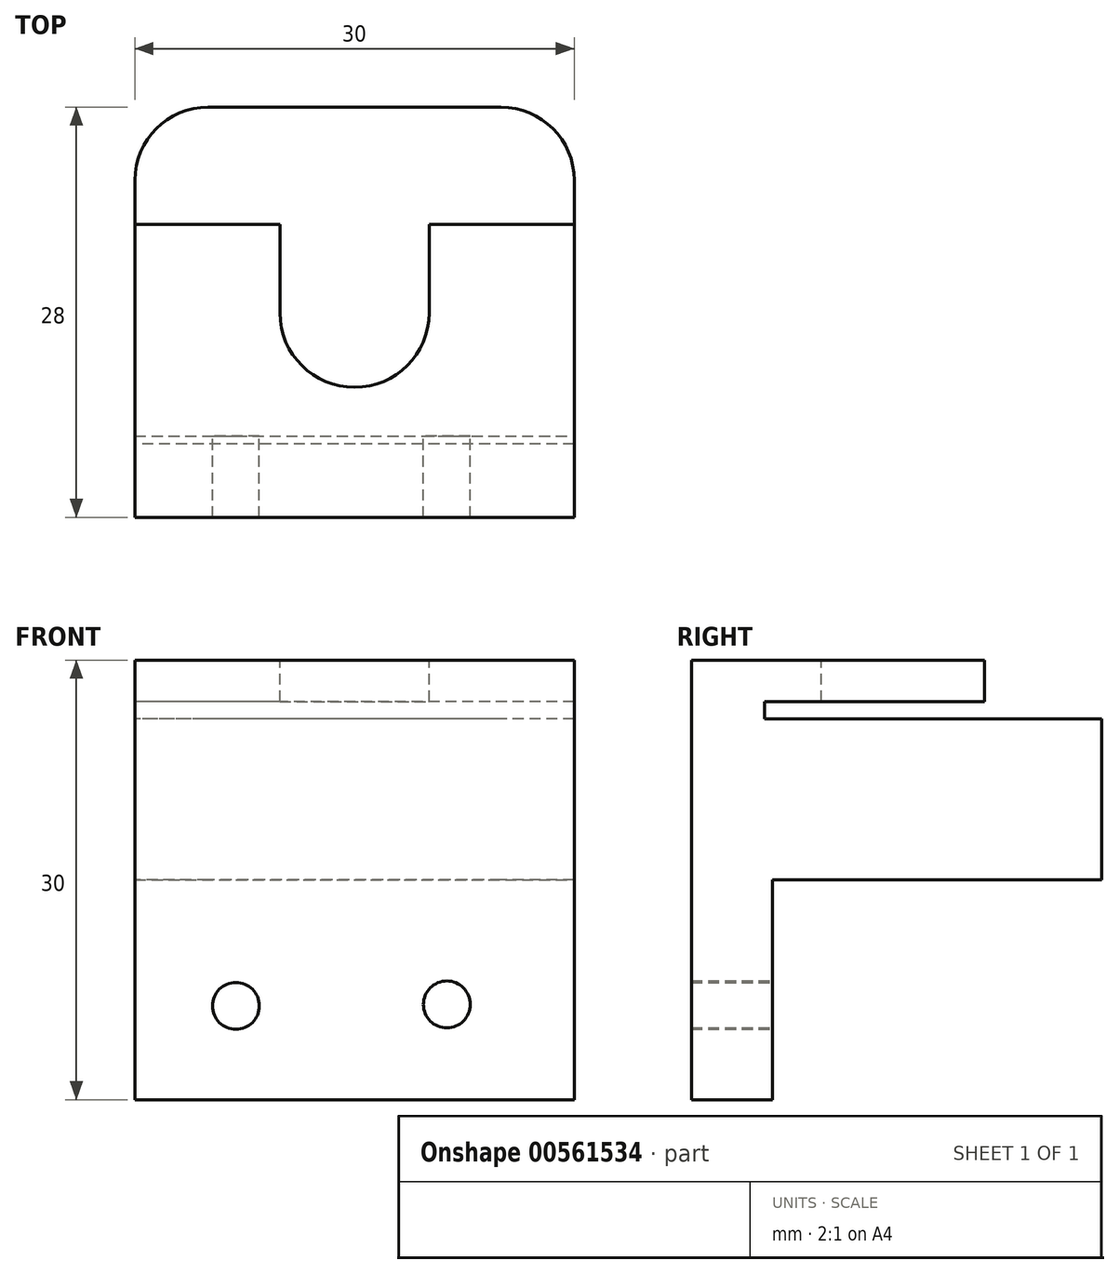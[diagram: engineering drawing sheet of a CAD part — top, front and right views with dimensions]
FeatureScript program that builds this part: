
annotation { "Feature Type Name" : "Feature", "Feature Type Description" : "" }
export const myFeature = defineFeature(function(context is Context, id is Id, definition is map)
    precondition{}
    {
        {
            var Q0;
            Q0=qCreatedBy(makeId("Top.planeOp"),FACE);
            var sketch = newSketch(context, id + "F0", { "sketchPlane" : qUnion([Q0])});
            skLineSegment(sketch, "E0.bottom", {"start": v(15, 14) * mm, "end": v(-15, 14) * mm});
            skLineSegment(sketch, "E0.top", {"start": v(15, -14) * mm, "end": v(-15, -14) * mm});
            skLineSegment(sketch, "E0.left", {"start": v(15, 14) * mm, "end": v(15, -14) * mm});
            skLineSegment(sketch, "E0.right", {"start": v(-15, 14) * mm, "end": v(-15, -14) * mm});
            skPoint(sketch, "E0.middle", {"position": v(0, 0) * mm});
            skSolve(sketch);
        }
        {
            var Q0;
            Q0=qSketchRegion(id+"F0",true);
            extrude(context, id + "F1", {"entities" : qUnion([Q0]), "depth" : 11 * mm, "offsetDistance" : 25 * mm});
        }
        {
            var Q0;
            Q0=makeQuery(id+"F1.opExtrude","SWEPT_EDGE",EDGE,{"disambiguationData":[OSD([sQuery(id+"F0.wireOp",EDGE,"E0.bottom"),sQuery(id+"F0.wireOp",EDGE,"E0.left")])]});
            var Q1;
            Q1=makeQuery(id+"F1.opExtrude","SWEPT_EDGE",EDGE,{"disambiguationData":[OSD([sQuery(id+"F0.wireOp",EDGE,"E0.bottom"),sQuery(id+"F0.wireOp",EDGE,"E0.right")])]});
            fillet(context, id + "F2", {"entities" : qUnion([Q0, Q1]), "radius" : 5 * mm, "tangentPropagation" : true, "allowEdgeOverflow" : false});
        }
        {
            var Q0;
            Q0=makeQuery(id+"F1.opExtrude","CAP_FACE",FACE,{"disambiguationData":[OSD([sQuery(id+"F0.wireOp",EDGE,"E0.bottom"),sQuery(id+"F0.wireOp",EDGE,"E0.top"),sQuery(id+"F0.wireOp",EDGE,"E0.left"),sQuery(id+"F0.wireOp",EDGE,"E0.right")])],"isStart":true});
            var sketch = newSketch(context, id + "F3", { "sketchPlane" : qUnion([Q0])});
            skLineSegment(sketch, "E1.bottom", {"start": v(-15, 14) * mm, "end": v(15, 14) * mm});
            skLineSegment(sketch, "E1.top", {"start": v(-15, 8.46) * mm, "end": v(15, 8.46) * mm});
            skLineSegment(sketch, "E1.left", {"start": v(-15, 14) * mm, "end": v(-15, 8.46) * mm});
            skLineSegment(sketch, "E1.right", {"start": v(15, 14) * mm, "end": v(15, 8.46) * mm});
            skPoint(sketch, "E1.middle", {"position": v(0, 11.23) * mm});
            skSolve(sketch);
        }
        {
            var Q0;
            Q0=qSketchRegion(id+"F3",true);
            extrude(context, id + "F4", {"entities" : qUnion([Q0]), "operationType" : NewBodyOperationType.ADD, "depth" : 15 * mm, "offsetDistance" : 25 * mm});
        }
        {
            var Q0;
            Q0=makeQuery(id+"F4.opExtrude","SWEPT_FACE",FACE,{"disambiguationData":[OSD([sQuery(id+"F3.wireOp",EDGE,"E1.top")])]});
            var sketch = newSketch(context, id + "F5", { "sketchPlane" : qUnion([Q0])});
            skCircle(sketch, "E2", {"center": v(-6.3, -8.5) * mm, "radius": 1.6 * mm});
            skCircle(sketch, "E3", {"center": v(8.1, -8.6) * mm, "radius": 1.6 * mm});
            skSolve(sketch);
        }
        {
            var Q0;
            Q0=qSketchRegion(id+"F5",true);
            extrude(context, id + "F6", {"entities" : qUnion([Q0]), "operationType" : NewBodyOperationType.REMOVE, "oppositeDirection" : true, "depth" : 16 * mm, "offsetDistance" : 25 * mm});
        }
        {
            var Q0;
            Q0=makeQuery(id+"F1.opExtrude","CAP_FACE",FACE,{"disambiguationData":[OSD([sQuery(id+"F0.wireOp",EDGE,"E0.bottom"),sQuery(id+"F0.wireOp",EDGE,"E0.top"),sQuery(id+"F0.wireOp",EDGE,"E0.left"),sQuery(id+"F0.wireOp",EDGE,"E0.right")])],"isStart":false});
            var sketch = newSketch(context, id + "F7", { "sketchPlane" : qUnion([Q0])});
            skLineSegment(sketch, "E4.bottom", {"start": v(15, -14) * mm, "end": v(-15, -14) * mm});
            skLineSegment(sketch, "E4.top", {"start": v(15, -9) * mm, "end": v(-15, -9) * mm});
            skLineSegment(sketch, "E4.left", {"start": v(15, -14) * mm, "end": v(15, -9) * mm});
            skLineSegment(sketch, "E4.right", {"start": v(-15, -14) * mm, "end": v(-15, -9) * mm});
            skPoint(sketch, "E4.middle", {"position": v(0, -11.5) * mm});
            skPoint(sketch, "E4.middle.positionSnap0", {"position": v(0, -14) * mm});
            skPoint(sketch, "E4.centerSnap0", {"position": v(0, -14) * mm});
            skSolve(sketch);
        }
        {
            var Q0;
            Q0=qSketchRegion(id+"F7",true);
            extrude(context, id + "F8", {"entities" : qUnion([Q0]), "operationType" : NewBodyOperationType.ADD, "depth" : 4 * mm, "offsetDistance" : 25 * mm});
        }
        {
            var Q0;
            Q0=makeQuery(id+"F8.opExtrude","SWEPT_FACE",FACE,{"disambiguationData":[OSD([sQuery(id+"F7.wireOp",EDGE,"E4.top")])]});
            var sketch = newSketch(context, id + "F9", { "sketchPlane" : qUnion([Q0])});
            skLineSegment(sketch, "E5.bottom", {"start": v(-15, 12.18) * mm, "end": v(15, 12.18) * mm});
            skLineSegment(sketch, "E5.top", {"start": v(-15, 15) * mm, "end": v(15, 15) * mm});
            skLineSegment(sketch, "E5.left", {"start": v(-15, 12.18) * mm, "end": v(-15, 15) * mm});
            skLineSegment(sketch, "E5.right", {"start": v(15, 12.18) * mm, "end": v(15, 15) * mm});
            skPoint(sketch, "E5.middle", {"position": v(0, 13.59) * mm});
            skSolve(sketch);
        }
        {
            var Q0;
            Q0=qSketchRegion(id+"F9",true);
            extrude(context, id + "F10", {"entities" : qUnion([Q0]), "operationType" : NewBodyOperationType.ADD, "depth" : 15 * mm, "offsetDistance" : 25 * mm});
        }
        {
            var Q0;
            Q0=makeQuery(id+"F10.opExtrude","SWEPT_FACE",FACE,{"disambiguationData":[OSD([sQuery(id+"F9.wireOp",EDGE,"E5.top")])]});
            var sketch = newSketch(context, id + "F11", { "sketchPlane" : qUnion([Q0])});
            skLineSegment(sketch, "E6", {"start": v(0.73, 5.65) * mm, "end": v(0.73, -8.35) * mm, "construction": true});
            skLineSegment(sketch, "E7", {"start": v(-8, -1.35) * mm, "end": v(8, -1.35) * mm, "construction": true});
            skLineSegment(sketch, "E8", {"start": v(-8, -0.05) * mm, "end": v(8, -0.05) * mm, "construction": true});
            skArc(sketch, "E9", {"start": v(-5.1, -0.05) * mm, "mid": v(0, -5.13) * mm, "end": v(5.1, -0.05) * mm});
            skPoint(sketch, "E9.startSnap0", {"position": v(-5.1, 0.45) * mm});
            skLineSegment(sketch, "E10", {"start": v(-5.1, -0.05) * mm, "end": v(-5.1, 5.65) * mm});
            skLineSegment(sketch, "E11", {"start": v(5.1, -0.05) * mm, "end": v(5.1, 5.65) * mm});
            skLineSegment(sketch, "E12", {"start": v(-5.1, 5.65) * mm, "end": v(-5.1, 6) * mm});
            skLineSegment(sketch, "E13", {"start": v(5.1, 5.65) * mm, "end": v(5.1, 6) * mm});
            skLineSegment(sketch, "E14", {"start": v(5.1, 6) * mm, "end": v(-5.1, 6) * mm});
            skSolve(sketch);
        }
        {
            var Q0;
            Q0 = qSketchRegion(id + "F11", true);
            extrude(context, id + "F12", {"entities" : qUnion([Q0]), "operationType" : NewBodyOperationType.REMOVE, "oppositeDirection" : true, "depth" : 3 * mm, "offsetDistance" : 25 * mm});
        }
    });
